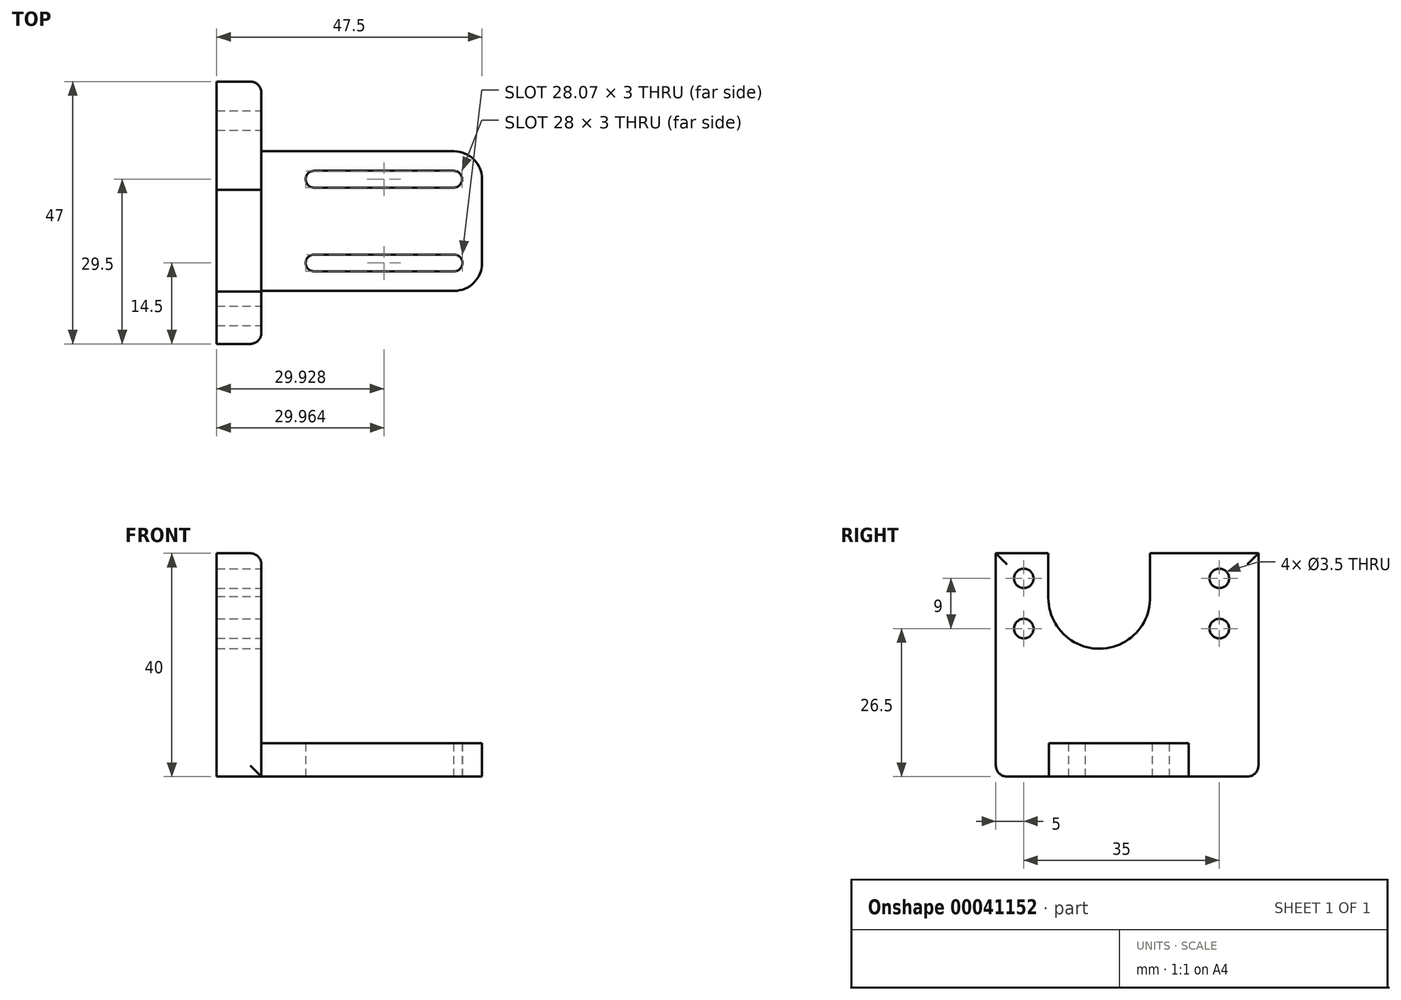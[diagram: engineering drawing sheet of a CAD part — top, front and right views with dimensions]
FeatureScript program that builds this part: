
annotation { "Feature Type Name" : "Feature", "Feature Type Description" : "" }
export const myFeature = defineFeature(function(context is Context, id is Id, definition is map)
    precondition{}
    {
        {
            var Q0;
            Q0=qCreatedBy(makeId("Top.planeOp"),FACE);
            var sketch = newSketch(context, id + "F0", { "sketchPlane" : qUnion([Q0])});
            skLineSegment(sketch, "E0.bottom", {"start": v(0, 0) * mm, "end": v(39.5, 0) * mm});
            skLineSegment(sketch, "E0.top", {"start": v(0, -25) * mm, "end": v(39.5, -25) * mm});
            skLineSegment(sketch, "E0.left", {"start": v(0, 0) * mm, "end": v(0, -25) * mm});
            skLineSegment(sketch, "E0.right", {"start": v(39.5, 0) * mm, "end": v(39.5, -25) * mm});
            skLineSegment(sketch, "E1", {"start": v(9.43, -3.5) * mm, "end": v(34.43, -3.5) * mm});
            skLineSegment(sketch, "E2.0", {"start": v(9.43, -6.5) * mm, "end": v(34.43, -6.5) * mm});
            skLineSegment(sketch, "E3.0", {"start": v(9.43, -18.5) * mm, "end": v(34.43, -18.5) * mm});
            skLineSegment(sketch, "E4.0", {"start": v(9.43, -21.5) * mm, "end": v(34.5, -21.5) * mm});
            skArc(sketch, "E5", {"start": v(34.43, -6.5) * mm, "mid": v(35.93, -5) * mm, "end": v(34.43, -3.5) * mm});
            skArc(sketch, "E6", {"start": v(34.5, -21.5) * mm, "mid": v(36, -19.96) * mm, "end": v(34.43, -18.5) * mm});
            skArc(sketch, "E7", {"start": v(9.43, -3.5) * mm, "mid": v(7.93, -5) * mm, "end": v(9.43, -6.5) * mm});
            skArc(sketch, "E8", {"start": v(9.43, -18.5) * mm, "mid": v(7.93, -20) * mm, "end": v(9.43, -21.5) * mm});
            skSolve(sketch);
        }
        {
            var Q0;
            Q0 = qSketchRegion(id + "F0", true);
            extrude(context, id + "F1", {"entities" : qUnion([Q0]), "depth" : 6 * mm});
        }
        {
            var Q0;
            Q0=makeQuery(id+"F1.opExtrude","SWEPT_EDGE",EDGE,{"disambiguationData":[OSD([sQuery(id+"F0.wireOp",EDGE,"E0.bottom"),sQuery(id+"F0.wireOp",EDGE,"E0.right")])]});
            var Q1;
            Q1=makeQuery(id+"F1.opExtrude","SWEPT_EDGE",EDGE,{"disambiguationData":[OSD([sQuery(id+"F0.wireOp",EDGE,"E0.top"),sQuery(id+"F0.wireOp",EDGE,"E0.right")])]});
            fillet(context, id + "F2", {"entities" : qUnion([Q0, Q1]), "radius" : 5 * mm, "tangentPropagation" : true, "allowEdgeOverflow" : false});
        }
        {
            var Q0;
            Q0=qCreatedBy(makeId("Top.planeOp"),FACE);
            var sketch = newSketch(context, id + "F3", { "sketchPlane" : qUnion([Q0])});
            skLineSegment(sketch, "E9.bottom", {"start": v(0, 12.5) * mm, "end": v(-8, 12.5) * mm});
            skLineSegment(sketch, "E9.top", {"start": v(0, -34.5) * mm, "end": v(-8, -34.5) * mm});
            skLineSegment(sketch, "E9.left", {"start": v(0, 12.5) * mm, "end": v(0, -34.5) * mm});
            skLineSegment(sketch, "E9.right", {"start": v(-8, 12.5) * mm, "end": v(-8, -34.5) * mm});
            skSolve(sketch);
        }
        {
            var Q0;
            Q0 = qSketchRegion(id + "F3", true);
            extrude(context, id + "F4", {"entities" : qUnion([Q0]), "operationType" : NewBodyOperationType.ADD, "depth" : 25 * mm});
        }
        {
            var Q0;
            Q0=makeQuery(id+"F1.opExtrude","CAP_EDGE",EDGE,{"disambiguationData":[OSD([sQuery(id+"F0.wireOp",EDGE,"E0.left")])],"isStart":false});
            var Q1;
            Q1=makeQuery(id+"F4.opExtrude","SWEPT_EDGE",EDGE,{"disambiguationData":[OSD([sQuery(id+"F3.wireOp",EDGE,"E9.top"),sQuery(id+"F3.wireOp",EDGE,"E9.left")])]});
            var Q2;
            Q2=makeQuery(id+"F4.opExtrude","SWEPT_EDGE",EDGE,{"disambiguationData":[OSD([sQuery(id+"F3.wireOp",EDGE,"E9.bottom"),sQuery(id+"F3.wireOp",EDGE,"E9.left")])]});
            fillet(context, id + "F5", {"entities" : qUnion([Q0, Q1, Q2]), "radius" : 7 * mm, "tangentPropagation" : true, "allowEdgeOverflow" : false});
        }
        {
            var Q0;
            Q0 = qSketchRegion(id + "F3", true);
            extrude(context, id + "F6", {"entities" : qUnion([Q0]), "operationType" : NewBodyOperationType.ADD, "depth" : 40 * mm});
        }
        {
            var Q0;
            Q0=qCreatedBy(makeId("Right.planeOp"),FACE);
            var sketch = newSketch(context, id + "F7", { "sketchPlane" : qUnion([Q0])});
            skCircle(sketch, "E10", {"center": v(-29.5, 35.5) * mm, "radius": 1.75 * mm});
            skCircle(sketch, "E11", {"center": v(5.5, 35.5) * mm, "radius": 1.75 * mm});
            skCircle(sketch, "E12", {"center": v(5.5, 26.5) * mm, "radius": 1.75 * mm});
            skCircle(sketch, "E13", {"center": v(-29.5, 26.5) * mm, "radius": 1.75 * mm});
            skCircle(sketch, "E14", {"center": v(-16, 32) * mm, "radius": 9.1 * mm});
            skLineSegment(sketch, "E15", {"start": v(-6.9, 32.29) * mm, "end": v(-6.9, 40.03) * mm});
            skLineSegment(sketch, "E16", {"start": v(-25.1, 32) * mm, "end": v(-25.1, 40.03) * mm});
            skLineSegment(sketch, "E17", {"start": v(-25.1, 40.03) * mm, "end": v(-6.9, 40.03) * mm});
            skSolve(sketch);
        }
        {
            var Q0;
            Q0 = qSketchRegion(id + "F7", true);
            extrude(context, id + "F8", {"entities" : qUnion([Q0]), "operationType" : NewBodyOperationType.REMOVE, "oppositeDirection" : true, "depth" : 25 * mm});
        }
        {
            var Q0;
            {var subQ0=sQuery(id+"F3.wireOp",EDGE,"E9.top");var subQ1=sQuery(id+"F3.wireOp",EDGE,"E9.left");Q0=makeQuery(id+"F8.boolean.opBoolean","SPLIT",EDGE,{"disambiguationData":[TD([makeQuery(id+"F4.opExtrude","SWEPT_FACE",FACE,{"disambiguationData":[OSD([subQ0])]})])],"derivedFrom":makeQuery(id+"F6.opExtrude","CAP_EDGE",EDGE,{"disambiguationData":[OSD([subQ1])],"isStart":false})});}
            var Q1;
            {var subQ0=sQuery(id+"F3.wireOp",EDGE,"E9.left");var subQ1=sQuery(id+"F3.wireOp",EDGE,"E9.bottom");Q1=makeQuery(id+"F8.boolean.opBoolean","SPLIT",EDGE,{"disambiguationData":[TD([makeQuery(id+"F4.opExtrude","SWEPT_FACE",FACE,{"disambiguationData":[OSD([subQ1])]})])],"derivedFrom":makeQuery(id+"F6.opExtrude","CAP_EDGE",EDGE,{"disambiguationData":[OSD([subQ0])],"isStart":false})});}
            var Q2;
            Q2=makeQuery(id+"F6.opExtrude","SWEPT_EDGE",EDGE,{"disambiguationData":[OSD([sQuery(id+"F3.wireOp",EDGE,"E9.top"),sQuery(id+"F3.wireOp",EDGE,"E9.left")])]});
            var Q3;
            Q3=makeQuery(id+"F6.opExtrude","SWEPT_EDGE",EDGE,{"disambiguationData":[OSD([sQuery(id+"F3.wireOp",EDGE,"E9.bottom"),sQuery(id+"F3.wireOp",EDGE,"E9.left")])]});
            var Q4;
            {var subQ0=sQuery(id+"F3.wireOp",EDGE,"E9.bottom");Q4=makeQuery(id+"F6.boolean.opBoolean","MERGE",EDGE,{"derivedFrom":[makeQuery(id+"F4.opExtrude","CAP_EDGE",EDGE,{"disambiguationData":[OSD([subQ0])],"isStart":true}),makeQuery(id+"F6.opExtrude","CAP_EDGE",EDGE,{"disambiguationData":[OSD([subQ0])],"isStart":true})]});}
            var Q5;
            {var subQ0=sQuery(id+"F3.wireOp",EDGE,"E9.top");Q5=makeQuery(id+"F6.boolean.opBoolean","MERGE",EDGE,{"derivedFrom":[makeQuery(id+"F4.opExtrude","CAP_EDGE",EDGE,{"disambiguationData":[OSD([subQ0])],"isStart":true}),makeQuery(id+"F6.opExtrude","CAP_EDGE",EDGE,{"disambiguationData":[OSD([subQ0])],"isStart":true})]});}
            fillet(context, id + "F9", {"entities" : qUnion([Q0, Q1, Q2, Q3, Q4, Q5]), "radius" : 2 * mm, "tangentPropagation" : true, "allowEdgeOverflow" : false});
        }
    });
